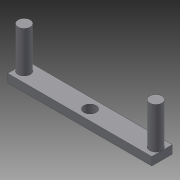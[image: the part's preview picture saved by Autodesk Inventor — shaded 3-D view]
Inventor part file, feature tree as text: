
AUTODESK INVENTOR PART (.ipt)
format: ipt  version: 2015 (Build 190159000, 159)  size: 97,280 bytes
history: native  units: mm
features: extrude x3, sketch x3, other x1
ambient origin geometry x8: Origin, YZ Plane, XZ Plane, XY Plane, X Axis, Y Axis, Z Axis, Center Point
bodies: Body1 (feature_tree)
feature tree (7):
  other  "ソリッド1"
  extrude  "押し出し1"  Depth=5.0mm
  extrude  "押し出し2"  Depth=35.0mm
  extrude  "押し出し3"  Depth=2.0mm TaperAngle=0.0deg
  sketch  "スケッチ1"
  sketch  "スケッチ2"
  sketch  "スケッチ3"
